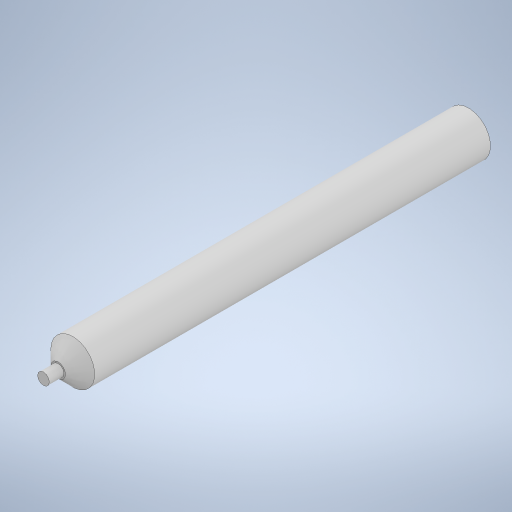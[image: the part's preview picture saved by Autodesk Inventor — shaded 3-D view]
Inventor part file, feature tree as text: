
AUTODESK INVENTOR PART (.ipt)
format: ipt  version: 2023 (Build 270158000, 158)  size: 235,008 bytes
history: native  units: in
note: dims shown in document units (in); Inventor stores cm internally (conversion verified against a paired STEP export)
features: extrude x2, sketch x2, chamfer x1
ambient origin geometry x8: Origin, YZ Plane, XZ Plane, XY Plane, X Axis, Y Axis, Z Axis, Center Point
bodies: Solid1 (feature_tree)
feature tree (5):
  extrude  "Extrusion1"  Depth=5.5118in TaperAngle=0.0deg
  extrude  "Extrusion2"  Depth=0.1969in TaperAngle=0.0deg
  chamfer  "Chamfer1"  Distance=0.1969in Angle=45.0deg
  sketch  "Sketch2"  dims[d0=0.5906in d1=5.5118in d2=0.0in]
  sketch  "Sketch3"  dims[d3=0.1575in d4=0.1969in d5=0.0in d6=0.1969in d7=0.0787in d8=45.0deg]
